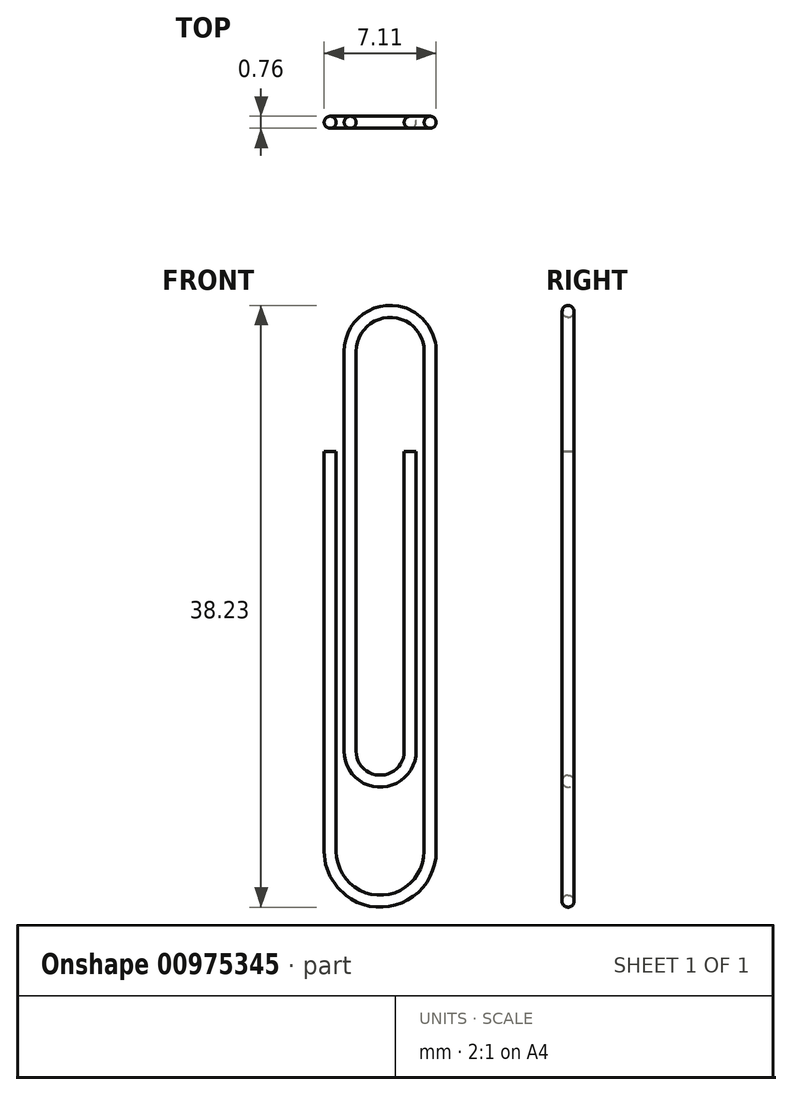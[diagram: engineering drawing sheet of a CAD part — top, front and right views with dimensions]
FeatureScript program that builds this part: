
annotation { "Feature Type Name" : "Feature", "Feature Type Description" : "" }
export const myFeature = defineFeature(function(context is Context, id is Id, definition is map)
    precondition{}
    {
        {
            var Q0;
            Q0=qCreatedBy(makeId("Front.planeOp"),FACE);
            var sketch = newSketch(context, id + "F0", { "sketchPlane" : qUnion([Q0])});
            skLineSegment(sketch, "E0", {"start": v(0, 0) * mm, "end": v(0, -25.4) * mm});
            skLineSegment(sketch, "E1", {"start": v(0, -25.4) * mm, "end": v(6.35, -25.4) * mm, "construction": true});
            skArc(sketch, "E2", {"start": v(0, -25.4) * mm, "mid": v(3.17, -28.58) * mm, "end": v(6.35, -25.4) * mm});
            skLineSegment(sketch, "E3", {"start": v(6.35, -25.4) * mm, "end": v(6.35, 6.35) * mm});
            skLineSegment(sketch, "E4", {"start": v(6.35, 6.35) * mm, "end": v(1.27, 6.35) * mm, "construction": true});
            skLineSegment(sketch, "E5", {"start": v(1.27, 6.35) * mm, "end": v(1.27, -19.05) * mm});
            skLineSegment(sketch, "E6", {"start": v(1.27, -19.05) * mm, "end": v(5.08, -19.05) * mm, "construction": true});
            skLineSegment(sketch, "E7", {"start": v(5.08, -19.05) * mm, "end": v(5.08, 0) * mm});
            skArc(sketch, "E8", {"start": v(1.27, -19.05) * mm, "mid": v(3.18, -20.96) * mm, "end": v(5.08, -19.05) * mm});
            skArc(sketch, "E9", {"start": v(6.35, 6.35) * mm, "mid": v(3.81, 8.89) * mm, "end": v(1.27, 6.35) * mm});
            skSolve(sketch);
        }
        {
            var Q0;
            Q0=qCreatedBy(makeId("Top.planeOp"),FACE);
            var sketch = newSketch(context, id + "F1", { "sketchPlane" : qUnion([Q0])});
            skCircle(sketch, "E10", {"center": v(0, 0) * mm, "radius": 0.38 * mm});
            skSolve(sketch);
        }
        {
            var Q0;
            Q0=makeQuery(id+"F1.imprint","IMPRINT",FACE,{"disambiguationData":[TD([[makeQuery(id+"F1.imprint","IMPRINT",EDGE,{"derivedFrom":sQuery(id+"F1.wireOp",EDGE,"E10")}),1.0]])]});
            var Q1;
            Q1=sQuery(id+"F0.wireOp",EDGE,"E0");
            var Q2;
            Q2=sQuery(id+"F0.wireOp",EDGE,"E2");
            var Q3;
            Q3=sQuery(id+"F0.wireOp",EDGE,"E3");
            var Q4;
            Q4=sQuery(id+"F0.wireOp",EDGE,"E9");
            var Q5;
            Q5=sQuery(id+"F0.wireOp",EDGE,"E5");
            var Q6;
            Q6=sQuery(id+"F0.wireOp",EDGE,"E8");
            var Q7;
            Q7=sQuery(id+"F0.wireOp",EDGE,"E7");
            sweep(context, id + "F2", {"profiles" : qUnion([Q0]), "path" : qUnion([Q1, Q2, Q3, Q4, Q5, Q6, Q7])});
        }
    });
